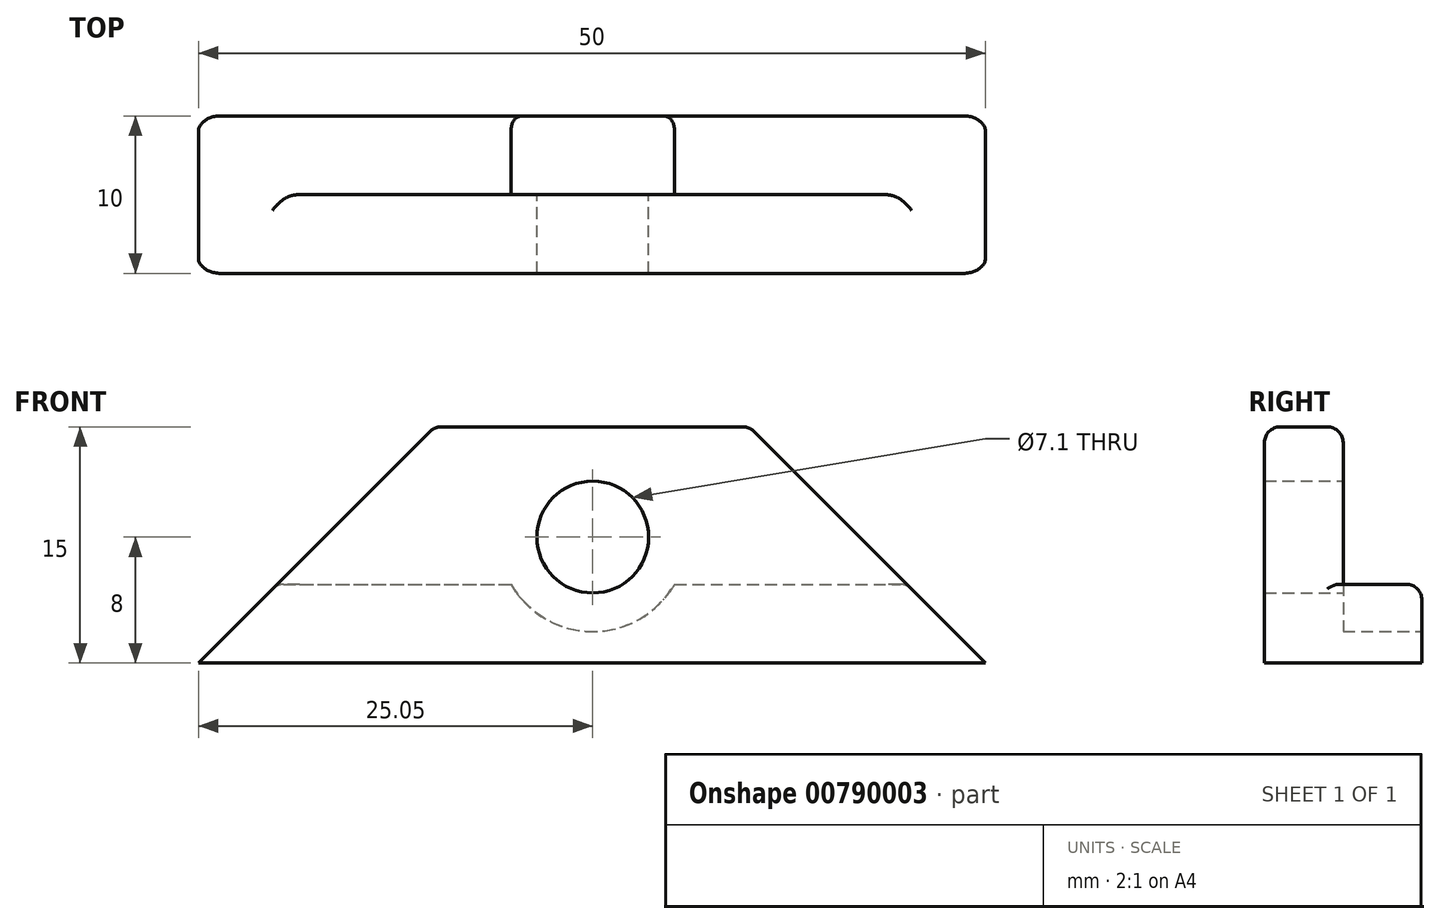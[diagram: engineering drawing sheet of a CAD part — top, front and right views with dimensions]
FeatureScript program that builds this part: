
annotation { "Feature Type Name" : "Feature", "Feature Type Description" : "" }
export const myFeature = defineFeature(function(context is Context, id is Id, definition is map)
    precondition{}
    {
        {
            var Q0;
            Q0=qCreatedBy(makeId("Top.planeOp"),FACE);
            var sketch = newSketch(context, id + "F0", { "sketchPlane" : qUnion([Q0])});
            skLineSegment(sketch, "E0.bottom", {"start": v(0.95, 0) * mm, "end": v(50.95, 0) * mm});
            skLineSegment(sketch, "E0.top", {"start": v(0.95, -10) * mm, "end": v(50.95, -10) * mm});
            skLineSegment(sketch, "E0.left", {"start": v(0.95, 0) * mm, "end": v(0.95, -10) * mm});
            skLineSegment(sketch, "E0.right", {"start": v(50.95, 0) * mm, "end": v(50.95, -10) * mm});
            skLineSegment(sketch, "E1", {"start": v(0.95, 0) * mm, "end": v(0.95, -5) * mm});
            skLineSegment(sketch, "E2", {"start": v(0.95, -5) * mm, "end": v(50.95, -5) * mm});
            skLineSegment(sketch, "E3", {"start": v(50.95, -5) * mm, "end": v(50.95, 0) * mm});
            skPoint(sketch, "E4", {"position": v(25.95, -10) * mm});
            skSolve(sketch);
        }
        {
            var Q0;
            Q0=makeQuery(id+"F0.imprint","IMPRINT",FACE,{"disambiguationData":[TD([[makeQuery(id+"F0.imprint","IMPRINT",EDGE,{"derivedFrom":sQuery(id+"F0.wireOp",EDGE,"E0.bottom")}),-1.0]])]});
            extrude(context, id + "F1", {"entities" : qUnion([Q0]), "depth" : 5 * mm, "offsetDistance" : 25 * mm});
        }
        {
            var Q0;
            Q0=makeQuery(id+"F0.imprint","IMPRINT",FACE,{"disambiguationData":[TD([[makeQuery(id+"F0.imprint","IMPRINT",EDGE,{"derivedFrom":sQuery(id+"F0.wireOp",EDGE,"E0.top")}),1.0]])]});
            extrude(context, id + "F2", {"entities" : qUnion([Q0]), "operationType" : NewBodyOperationType.ADD, "depth" : 15 * mm, "offsetDistance" : 25 * mm});
        }
        {
            var Q0;
            Q0=makeQuery(id+"F2.opExtrude","CAP_EDGE",EDGE,{"disambiguationData":[OSD([sQuery(id+"F0.wireOp",EDGE,"E0.right")])],"isStart":false});
            var Q1;
            Q1=makeQuery(id+"F2.opExtrude","CAP_EDGE",EDGE,{"disambiguationData":[OSD([sQuery(id+"F0.wireOp",EDGE,"E0.left")])],"isStart":false});
            chamfer(context, id + "F3", {"entities" : qUnion([Q0, Q1]), "chamferType" : ChamferType.OFFSET_ANGLE, "width" : 15 * mm, "oppositeDirection" : false, "angle" : 45 * degree, "tangentPropagation" : true});
        }
        {
            var Q0;
            Q0=qCreatedBy(makeId("Front.planeOp"),FACE);
            var sketch = newSketch(context, id + "F4", { "sketchPlane" : qUnion([Q0])});
            skLineSegment(sketch, "E5", {"start": v(0, 0) * mm, "end": v(51, 0) * mm});
            skPoint(sketch, "E6", {"position": v(26, 0) * mm});
            skLineSegment(sketch, "E7", {"start": v(26, 0) * mm, "end": v(26, 8) * mm});
            skSolve(sketch);
        }
        {
            var Q0;
            Q0=sQuery(id+"F4.wireOp",VERTEX,"E7.end");
            var Q1;
            Q1=makeQuery(id+"F1.opExtrude","SWEPT_BODY",BODY,{"disambiguationData":[OSD([sQuery(id+"F0.wireOp",EDGE,"E0.bottom"),sQuery(id+"F0.wireOp",EDGE,"E1"),sQuery(id+"F0.wireOp",EDGE,"E2"),sQuery(id+"F0.wireOp",EDGE,"E3")])]});
            hole(context, id + "F5", {"style" : HoleStyle.C_BORE, "endStyle" : HoleEndStyle.THROUGH, "oppositeDirection" : true, "holeDiameter" : 7.1 * mm, "cBoreDiameter" : 12 * mm, "cBoreDepth" : 0 * mm, "majorDiameter" : 5 * mm, "isTappedThrough" : true, "tappedDepth" : 12 * mm, "tapClearance" : 3, "locations" : qUnion([Q0]), "scope" : qUnion([Q1])});
        }
        {
            var Q0;
            {var subQ0=sQuery(id+"F0.wireOp",EDGE,"E0.right");Q0=makeQuery(id+"F3.opChamfer","BLEND_EDGE",EDGE,{"blendedFrom":[makeQuery(id+"F2.opExtrude","CAP_EDGE",EDGE,{"disambiguationData":[OSD([subQ0])],"isStart":false}),makeQuery(id+"F2.opExtrude","CAP_FACE",FACE,{"disambiguationData":[OSD([sQuery(id+"F0.wireOp",EDGE,"E0.top"),sQuery(id+"F0.wireOp",EDGE,"E0.left"),subQ0,sQuery(id+"F0.wireOp",EDGE,"E2")])],"isStart":false})],"blendedInto":[makeQuery(id+"F2.opExtrude","CAP_FACE",FACE,{"disambiguationData":[OSD([sQuery(id+"F0.wireOp",EDGE,"E0.top"),sQuery(id+"F0.wireOp",EDGE,"E0.left"),subQ0,sQuery(id+"F0.wireOp",EDGE,"E2")])],"isStart":false})]});}
            var Q1;
            {var subQ0=sQuery(id+"F0.wireOp",EDGE,"E0.left");Q1=makeQuery(id+"F3.opChamfer","BLEND_EDGE",EDGE,{"blendedFrom":[makeQuery(id+"F2.opExtrude","CAP_EDGE",EDGE,{"disambiguationData":[OSD([subQ0])],"isStart":false}),makeQuery(id+"F2.opExtrude","CAP_FACE",FACE,{"disambiguationData":[OSD([sQuery(id+"F0.wireOp",EDGE,"E0.top"),subQ0,sQuery(id+"F0.wireOp",EDGE,"E0.right"),sQuery(id+"F0.wireOp",EDGE,"E2")])],"isStart":false})],"blendedInto":[makeQuery(id+"F2.opExtrude","CAP_FACE",FACE,{"disambiguationData":[OSD([sQuery(id+"F0.wireOp",EDGE,"E0.top"),subQ0,sQuery(id+"F0.wireOp",EDGE,"E0.right"),sQuery(id+"F0.wireOp",EDGE,"E2")])],"isStart":false})]});}
            var Q2;
            Q2=makeQuery(id+"F2.opExtrude","CAP_EDGE",EDGE,{"disambiguationData":[OSD([sQuery(id+"F0.wireOp",EDGE,"E2")])],"isStart":false});
            var Q3;
            Q3=makeQuery(id+"F2.opExtrude","CAP_EDGE",EDGE,{"disambiguationData":[OSD([sQuery(id+"F0.wireOp",EDGE,"E0.top")])],"isStart":false});
            var Q4;
            Q4=makeQuery(id+"F3.opChamfer","BLEND_EDGE",EDGE,{"blendedFrom":[makeQuery(id+"F2.opExtrude","CAP_EDGE",EDGE,{"disambiguationData":[OSD([sQuery(id+"F0.wireOp",EDGE,"E0.left")])],"isStart":false}),makeQuery(id+"F2.opExtrude","SWEPT_FACE",FACE,{"disambiguationData":[OSD([sQuery(id+"F0.wireOp",EDGE,"E2")])]})],"blendedInto":[makeQuery(id+"F2.opExtrude","SWEPT_FACE",FACE,{"disambiguationData":[OSD([sQuery(id+"F0.wireOp",EDGE,"E2")])]})]});
            var Q5;
            Q5=makeQuery(id+"F3.opChamfer","BLEND_EDGE",EDGE,{"blendedFrom":[makeQuery(id+"F2.opExtrude","CAP_EDGE",EDGE,{"disambiguationData":[OSD([sQuery(id+"F0.wireOp",EDGE,"E0.left")])],"isStart":false}),makeQuery(id+"F2.opExtrude","SWEPT_FACE",FACE,{"disambiguationData":[OSD([sQuery(id+"F0.wireOp",EDGE,"E0.top")])]})],"blendedInto":[makeQuery(id+"F2.opExtrude","SWEPT_FACE",FACE,{"disambiguationData":[OSD([sQuery(id+"F0.wireOp",EDGE,"E0.top")])]})]});
            var Q6;
            Q6=makeQuery(id+"F3.opChamfer","BLEND_EDGE",EDGE,{"blendedFrom":[makeQuery(id+"F2.opExtrude","CAP_EDGE",EDGE,{"disambiguationData":[OSD([sQuery(id+"F0.wireOp",EDGE,"E0.left")])],"isStart":false}),makeQuery(id+"F1.opExtrude","CAP_FACE",FACE,{"disambiguationData":[OSD([sQuery(id+"F0.wireOp",EDGE,"E0.bottom"),sQuery(id+"F0.wireOp",EDGE,"E1"),sQuery(id+"F0.wireOp",EDGE,"E2"),sQuery(id+"F0.wireOp",EDGE,"E3")])],"isStart":false})],"blendedInto":[makeQuery(id+"F1.opExtrude","CAP_FACE",FACE,{"disambiguationData":[OSD([sQuery(id+"F0.wireOp",EDGE,"E0.bottom"),sQuery(id+"F0.wireOp",EDGE,"E1"),sQuery(id+"F0.wireOp",EDGE,"E2"),sQuery(id+"F0.wireOp",EDGE,"E3")])],"isStart":false})]});
            var Q7;
            Q7=makeQuery(id+"F3.opChamfer","BLEND_EDGE",EDGE,{"blendedFrom":[makeQuery(id+"F2.opExtrude","CAP_EDGE",EDGE,{"disambiguationData":[OSD([sQuery(id+"F0.wireOp",EDGE,"E0.right")])],"isStart":false}),makeQuery(id+"F1.opExtrude","CAP_FACE",FACE,{"disambiguationData":[OSD([sQuery(id+"F0.wireOp",EDGE,"E0.bottom"),sQuery(id+"F0.wireOp",EDGE,"E1"),sQuery(id+"F0.wireOp",EDGE,"E2"),sQuery(id+"F0.wireOp",EDGE,"E3")])],"isStart":false})],"blendedInto":[makeQuery(id+"F1.opExtrude","CAP_FACE",FACE,{"disambiguationData":[OSD([sQuery(id+"F0.wireOp",EDGE,"E0.bottom"),sQuery(id+"F0.wireOp",EDGE,"E1"),sQuery(id+"F0.wireOp",EDGE,"E2"),sQuery(id+"F0.wireOp",EDGE,"E3")])],"isStart":false})]});
            var Q8;
            Q8=makeQuery(id+"F3.opChamfer","BLEND_EDGE",EDGE,{"blendedFrom":[makeQuery(id+"F2.opExtrude","CAP_EDGE",EDGE,{"disambiguationData":[OSD([sQuery(id+"F0.wireOp",EDGE,"E0.right")])],"isStart":false}),makeQuery(id+"F2.opExtrude","SWEPT_FACE",FACE,{"disambiguationData":[OSD([sQuery(id+"F0.wireOp",EDGE,"E2")])]})],"blendedInto":[makeQuery(id+"F2.opExtrude","SWEPT_FACE",FACE,{"disambiguationData":[OSD([sQuery(id+"F0.wireOp",EDGE,"E2")])]})]});
            var Q9;
            Q9=makeQuery(id+"F3.opChamfer","BLEND_EDGE",EDGE,{"blendedFrom":[makeQuery(id+"F2.opExtrude","CAP_EDGE",EDGE,{"disambiguationData":[OSD([sQuery(id+"F0.wireOp",EDGE,"E0.right")])],"isStart":false}),makeQuery(id+"F2.opExtrude","SWEPT_FACE",FACE,{"disambiguationData":[OSD([sQuery(id+"F0.wireOp",EDGE,"E0.top")])]})],"blendedInto":[makeQuery(id+"F2.opExtrude","SWEPT_FACE",FACE,{"disambiguationData":[OSD([sQuery(id+"F0.wireOp",EDGE,"E0.top")])]})]});
            var Q10;
            Q10=makeQuery(id+"F1.opExtrude","CAP_EDGE",EDGE,{"disambiguationData":[OSD([sQuery(id+"F0.wireOp",EDGE,"E0.bottom")])],"isStart":false});
            var Q11;
            Q11=makeQuery(id+"F1.opExtrude","CAP_EDGE",EDGE,{"disambiguationData":[OSD([sQuery(id+"F0.wireOp",EDGE,"E2")])],"isStart":false});
            var Q12;
            Q12=makeQuery(id+"F3.opChamfer","BLEND_EDGE",EDGE,{"blendedFrom":[makeQuery(id+"F2.opExtrude","CAP_EDGE",EDGE,{"disambiguationData":[OSD([sQuery(id+"F0.wireOp",EDGE,"E0.right")])],"isStart":false}),makeQuery(id+"F1.opExtrude","SWEPT_FACE",FACE,{"disambiguationData":[OSD([sQuery(id+"F0.wireOp",EDGE,"E0.bottom")])]})],"blendedInto":[makeQuery(id+"F1.opExtrude","SWEPT_FACE",FACE,{"disambiguationData":[OSD([sQuery(id+"F0.wireOp",EDGE,"E0.bottom")])]})]});
            var Q13;
            Q13=makeQuery(id+"F3.opChamfer","BLEND_EDGE",EDGE,{"blendedFrom":[makeQuery(id+"F2.opExtrude","CAP_EDGE",EDGE,{"disambiguationData":[OSD([sQuery(id+"F0.wireOp",EDGE,"E0.left")])],"isStart":false}),makeQuery(id+"F1.opExtrude","SWEPT_FACE",FACE,{"disambiguationData":[OSD([sQuery(id+"F0.wireOp",EDGE,"E0.bottom")])]})],"blendedInto":[makeQuery(id+"F1.opExtrude","SWEPT_FACE",FACE,{"disambiguationData":[OSD([sQuery(id+"F0.wireOp",EDGE,"E0.bottom")])]})]});
            var Q14;
            Q14=makeQuery(id+"F5.hole-0.boolean.opBoolean","INTERSECT",EDGE,{"disambiguationData":[OD(1.0)],"derivedFrom":[makeQuery(id+"F1.opExtrude","CAP_FACE",FACE,{"disambiguationData":[OSD([sQuery(id+"F0.wireOp",EDGE,"E0.bottom"),sQuery(id+"F0.wireOp",EDGE,"E1"),sQuery(id+"F0.wireOp",EDGE,"E2"),sQuery(id+"F0.wireOp",EDGE,"E3")])],"isStart":false}),makeQuery(id+"F5.hole-0.opRevolve","SWEPT_FACE",FACE,{"disambiguationData":[OSD([sQuery(id+"F5.hole-0.sketch.wireOp",EDGE,"cbore_start_line_2")])]})]});
            var Q15;
            Q15=makeQuery(id+"F5.hole-0.boolean.opBoolean","COPY",EDGE,{"derivedFrom":makeQuery(id+"F5.hole-0.opRevolve","SWEPT_EDGE",EDGE,{"disambiguationData":[OSD([sQuery(id+"F5.hole-0.sketch.wireOp",EDGE,"cbore_start_line_2"),sQuery(id+"F5.hole-0.sketch.wireOp",EDGE,"cbore_start_line_3")])]})});
            var Q16;
            Q16=makeQuery(id+"F5.hole-0.boolean.opBoolean","INTERSECT",EDGE,{"disambiguationData":[OD(0.0)],"derivedFrom":[makeQuery(id+"F1.opExtrude","CAP_FACE",FACE,{"disambiguationData":[OSD([sQuery(id+"F0.wireOp",EDGE,"E0.bottom"),sQuery(id+"F0.wireOp",EDGE,"E1"),sQuery(id+"F0.wireOp",EDGE,"E2"),sQuery(id+"F0.wireOp",EDGE,"E3")])],"isStart":false}),makeQuery(id+"F5.hole-0.opRevolve","SWEPT_FACE",FACE,{"disambiguationData":[OSD([sQuery(id+"F5.hole-0.sketch.wireOp",EDGE,"cbore_start_line_2")])]})]});
            fillet(context, id + "F6", {"entities" : qUnion([Q0, Q1, Q2, Q3, Q4, Q5, Q6, Q7, Q8, Q9, Q10, Q11, Q12, Q13, Q14, Q15, Q16]), "radius" : 1 * mm, "tangentPropagation" : true, "allowEdgeOverflow" : false});
        }
    });
